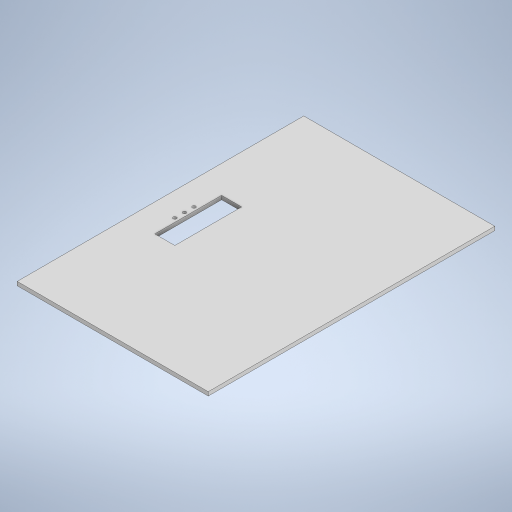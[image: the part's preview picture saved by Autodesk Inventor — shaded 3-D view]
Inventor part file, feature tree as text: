
AUTODESK INVENTOR PART (.ipt)
format: ipt  version: 2023 (Build 270158000, 158)  size: 272,896 bytes
history: native  units: mm
features: extrude x1, sketch x1
ambient origin geometry x8: Origin, YZ Plane, XZ Plane, XY Plane, X Axis, Y Axis, Z Axis, Center Point
bodies: Body1 (feature_tree)
feature tree (2):
  extrude  "Выдавливание2"  Depth=600.0mm
  sketch  "Эскиз1"
